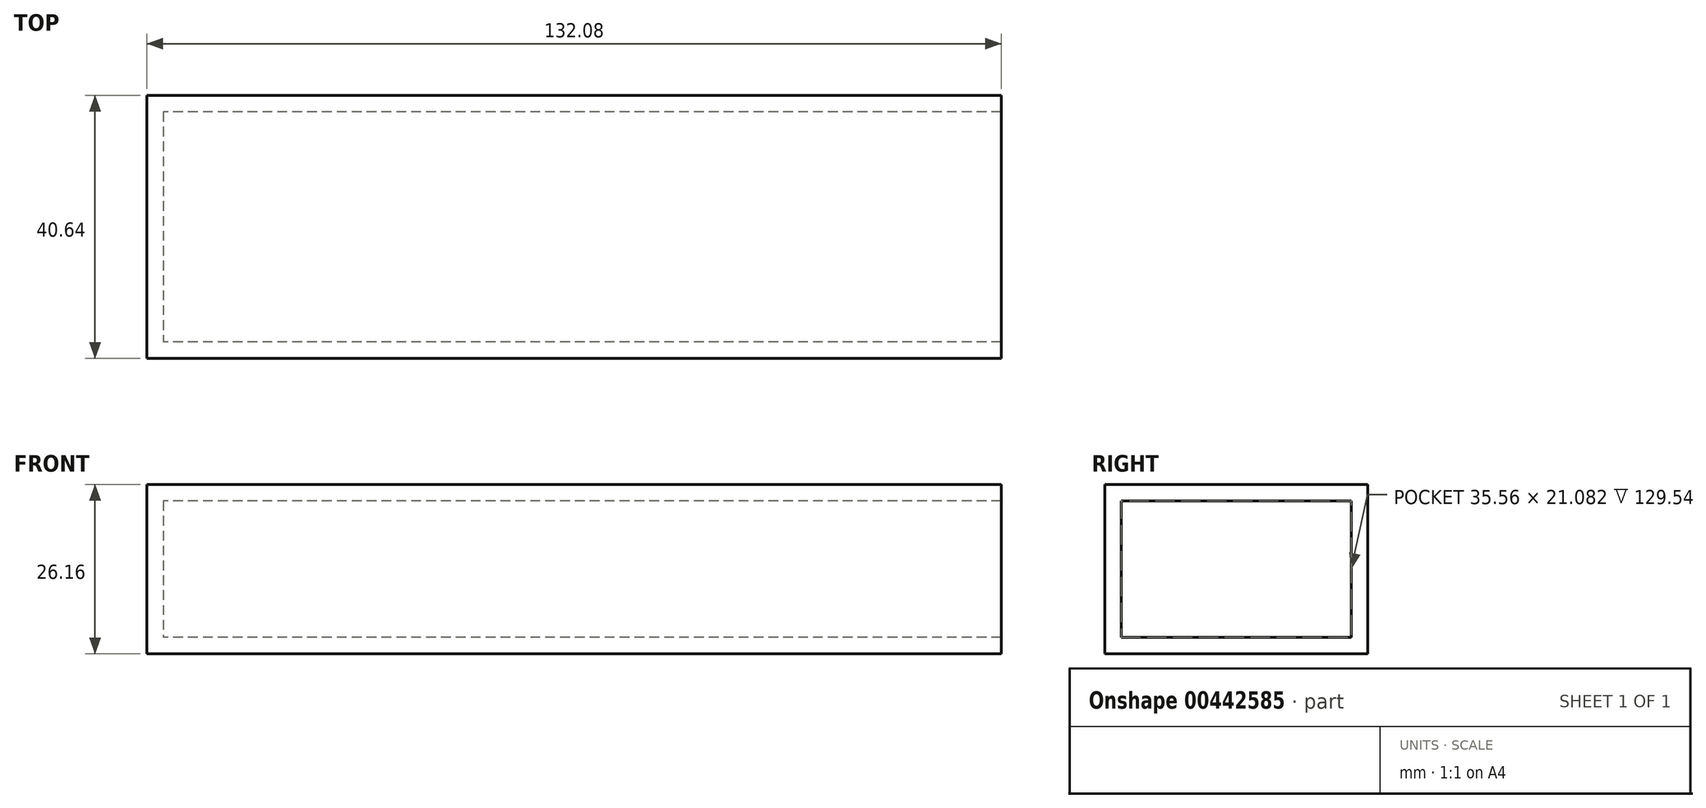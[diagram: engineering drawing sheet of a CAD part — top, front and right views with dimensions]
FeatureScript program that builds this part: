
annotation { "Feature Type Name" : "Feature", "Feature Type Description" : "" }
export const myFeature = defineFeature(function(context is Context, id is Id, definition is map)
    precondition{}
    {
        {
            var Q0;
            Q0=qCreatedBy(makeId("Top.planeOp"),FACE);
            var sketch = newSketch(context, id + "F0", { "sketchPlane" : qUnion([Q0])});
            skLineSegment(sketch, "E0.bottom", {"start": v(66.04, 20.32) * mm, "end": v(-66.04, 20.32) * mm});
            skLineSegment(sketch, "E0.top", {"start": v(66.04, -20.32) * mm, "end": v(-66.04, -20.32) * mm});
            skLineSegment(sketch, "E0.left", {"start": v(66.04, 20.32) * mm, "end": v(66.04, -20.32) * mm});
            skLineSegment(sketch, "E0.right", {"start": v(-66.04, 20.32) * mm, "end": v(-66.04, -20.32) * mm});
            skPoint(sketch, "E0.middle", {"position": v(0, 0) * mm});
            skSolve(sketch);
        }
        {
            var Q0;
            Q0 = qSketchRegion(id + "F0", true);
            extrude(context, id + "F1", {"entities" : qUnion([Q0]), "depth" : 26.16 * mm, "offsetDistance" : 25.4 * mm});
        }
        {
            var Q0;
            Q0=makeQuery(id+"F1.opExtrude","SWEPT_FACE",FACE,{"disambiguationData":[OSD([sQuery(id+"F0.wireOp",EDGE,"E0.left")])]});
            shell(context, id + "F2", {"entities" : qUnion([Q0]), "thickness" : 2.54 * mm});
        }
    });
